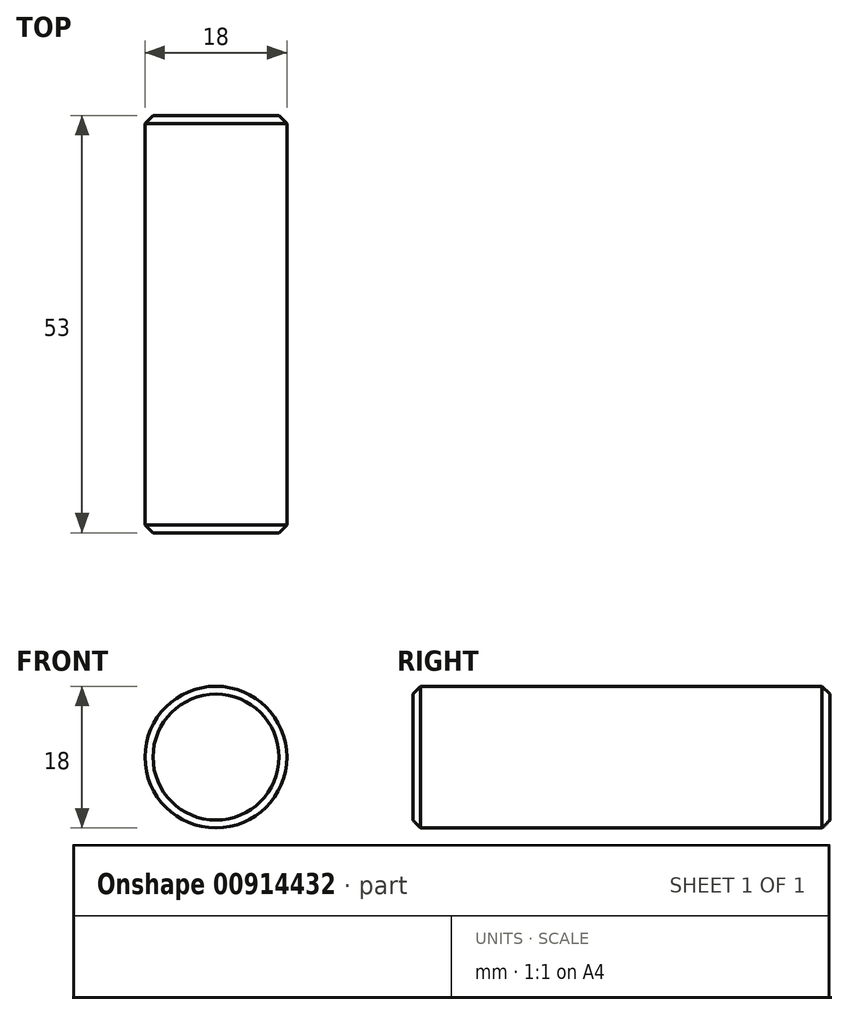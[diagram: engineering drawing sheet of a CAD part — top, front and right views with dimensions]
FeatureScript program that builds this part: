
annotation { "Feature Type Name" : "Feature", "Feature Type Description" : "" }
export const myFeature = defineFeature(function(context is Context, id is Id, definition is map)
    precondition{}
    {
        {
            var Q0;
            Q0=qCreatedBy(makeId("Front.planeOp"),FACE);
            var sketch = newSketch(context, id + "F0", { "sketchPlane" : qUnion([Q0])});
            skCircle(sketch, "E0", {"center": v(0, 0) * mm, "radius": 9 * mm});
            skSolve(sketch);
        }
        {
            var Q0;
            Q0=makeQuery(id+"F0.imprint","IMPRINT",FACE,{"disambiguationData":[TD([[makeQuery(id+"F0.imprint","IMPRINT",EDGE,{"derivedFrom":sQuery(id+"F0.wireOp",EDGE,"E0")}),1.0]])]});
            extrude(context, id + "F1", {"entities" : qUnion([Q0]), "depth" : 53 * mm, "offsetDistance" : 25 * mm});
        }
        {
            var Q0;
            Q0=makeQuery(id+"F1.opExtrude","SWEPT_FACE",FACE,{"disambiguationData":[OSD([sQuery(id+"F0.wireOp",EDGE,"E0")])]});
            chamfer(context, id + "F2", {"entities" : qUnion([Q0]), "width" : 1 * mm, "tangentPropagation" : true});
        }
    });
